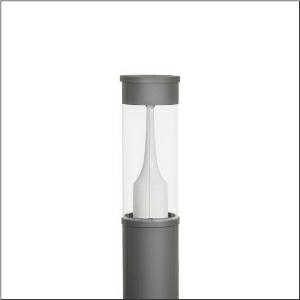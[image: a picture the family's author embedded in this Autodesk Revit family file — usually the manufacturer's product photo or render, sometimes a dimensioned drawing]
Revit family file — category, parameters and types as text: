
# Revit family: city-light_120_iq___pl1_2s_5xa5285jf14h_c322
name_source: partatom
category: Lighting Fixtures
units: mm (PartAtom-declared; Revit-internal decimal feet)

## family parameters
Cut with Voids When Loaded = No
Host = Face
Light Source = No
Part Type = Normal
Room Calculation Point = No
Round Connector Dimension = Use Diameter
Shared = No

## types (1)
- --- (1 x LED, 2970 lm, 19.3 W, 3000K)
    Apparent Load = 19 VA
    CIE Flux Codes = 23 62 94 96 100
    Color Rendering = 70
    Color Temperature = 3000K
    Default Elevation = 1800 mm
    Description = City-Light 120 iQ, bollard luminaire, Module 540 iQ-SR, primary light control with 3 zone facetted reflector, of plastic, silver coated, highly specular, structured, primary optical cover: cover, of PMMA, transparent, light distribution: PL1.2s, primary light characteristic: symmetric, LED, High Power LED, rated luminous flux: 2.970lm, luminous efficacy: 154lm/W, light colour: 730, colour temperature: 3000K, control gear: iQ Street-Remote, control: Auto-Match, Temp-Guard, Lumen-Switch, Night-Set, Smart-Wire, Light-Fading, Desk-Remote (wireless, voltage-free reading and setting of iQ features in the workshop via application-optimized NFC function/RFID function), optimised constant luminous flux control (CLO 2.0), Street-Remote, pre-setting: logarithmic dimming characteristic, with terminal, 6-pole, max. 2.5mm², mains connection: 230..240V, AC, 50/60Hz, start of lifetime: 19W, end of service life: 21W, reduction: 10W, luminaire housing, cylindrical, of extruded aluminium section, coated, Siteco® metallic grey (DB 702S), length: 1.200mm, diameter: 200mm, Module 540 iQ-SR, traffic white (RAL 9016), equipment: standard, protection rating (complete): IP54, insulation class (complete): insulation class II (safety insulation), certification: CE, ENEC, VDE, packaging unit: 1 piece

Light Distribution: PL1.2s
    Height = 500 mm
    Lamp = 1 x LED
    Lamp Light Flux = 2970 lm
    Lamp Power = 19.3 W
    Lamp count = 1
    Length = 200 mm  [stored 0.656168 ft]
    Luminous efficacy = 154 lm/W
    Manufacturer = Siteco
    ModVariant = No
    Model = 5XA5285JF14H
    Mounting Place = Floor
    Mounting Type = Freestanding
    Number of Poles = 1
    OnlyDefault = Yes
    Power Factor = 1
    Product Name = City-Light 120 iQ | PL1.2s
    Product group = bollard luminaire
    ProductGroupID = 1304
    Protection Class = Protection class II
    Protection Degree = IP 54
    RLX_Detail_Level = 1
    RLX_Emergency_Light_Flux = 0 lm
    RLX_Emergency_Type = 0
    RLX_Emergency_Type_DB = No
    RlxData = <blob elided: 30213 chars, md5=96f5a210>
    Socket = socket
    Standby Power = 0 W
    System Light Flux = 2970 lm
    System Power = 19 W
    Type Comments = factory setting: luminous flux: 100 % | dim-lin: 254 | 403 mA
    Type Image = l_1006922.jpg
    URL = http://relux.com
    VarID = @adj_144689
    Voltage = 0 V
    Weight = 0.00 kg
    Width = 0 mm  [stored 0 ft]

note: [stored X ft] marks values corroborated as IEEE doubles in the binary element streams (Revit-internal decimal feet)

## geometry (parser evidence)
native form markers: Blend x4, Sweep x8
no freeform markers — native parametric forms only
